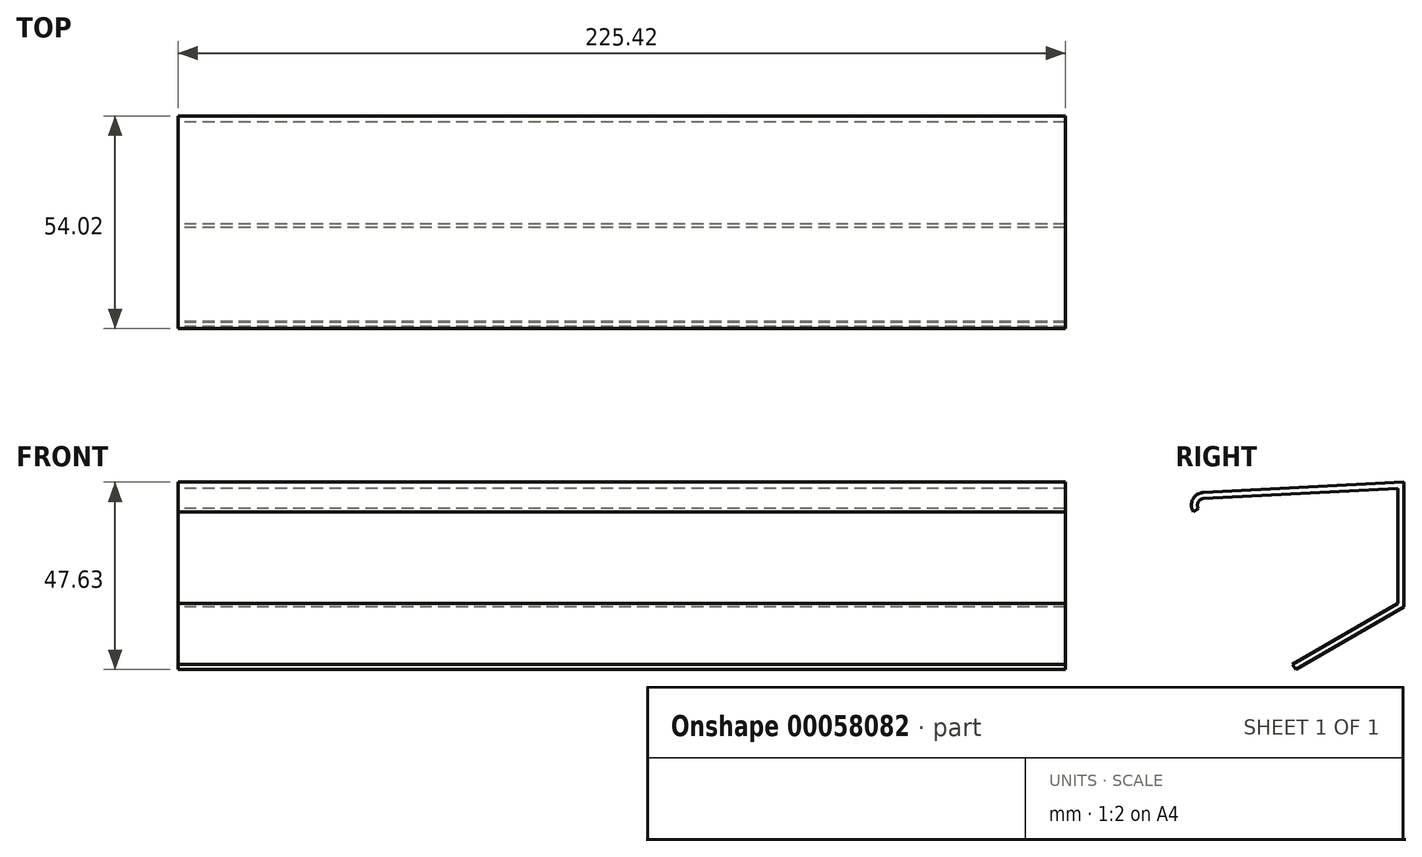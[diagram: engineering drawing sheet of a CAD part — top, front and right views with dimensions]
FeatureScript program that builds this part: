
annotation { "Feature Type Name" : "Feature", "Feature Type Description" : "" }
export const myFeature = defineFeature(function(context is Context, id is Id, definition is map)
    precondition{}
    {
        {
            var Q0;
            Q0=qCreatedBy(makeId("Right.planeOp"),FACE);
            var sketch = newSketch(context, id + "F0", { "sketchPlane" : qUnion([Q0])});
            skLineSegment(sketch, "E0", {"start": v(0, 0) * mm, "end": v(0, 31.75) * mm});
            skLineSegment(sketch, "E1", {"start": v(-56.5, 28.79) * mm, "end": v(-27.5, -15.88) * mm});
            skLineSegment(sketch, "E2", {"start": v(-27.5, -15.87) * mm, "end": v(0, 0) * mm});
            skLineSegment(sketch, "E3", {"start": v(0, 31.75) * mm, "end": v(-56.5, 28.79) * mm});
            skSolve(sketch);
        }
        {
            var Q0;
            Q0=makeQuery(id+"F0.imprint","IMPRINT",FACE,{"disambiguationData":[TD([[makeQuery(id+"F0.imprint","IMPRINT",EDGE,{"derivedFrom":sQuery(id+"F0.wireOp",EDGE,"E0")}),1.0]])]});
            extrude(context, id + "F1", {"entities" : qUnion([Q0]), "endBound" : BoundingType.SYMMETRIC, "depth" : 225.42 * mm});
        }
        {
            var Q0;
            Q0=makeQuery(id+"F1.opExtrude","SWEPT_EDGE",EDGE,{"disambiguationData":[OSD([sQuery(id+"F0.wireOp",EDGE,"E1"),sQuery(id+"F0.wireOp",EDGE,"E3")])]});
            fillet(context, id + "F2", {"entities" : qUnion([Q0]), "radius" : 3.17 * mm, "tangentPropagation" : true, "allowEdgeOverflow" : false});
        }
        {
            var Q0;
            Q0=makeQuery(id+"F1.opExtrude","CAP_FACE",FACE,{"disambiguationData":[OSD([sQuery(id+"F0.wireOp",EDGE,"E0"),sQuery(id+"F0.wireOp",EDGE,"E1"),sQuery(id+"F0.wireOp",EDGE,"E2"),sQuery(id+"F0.wireOp",EDGE,"E3")])],"isStart":false});
            var Q1;
            Q1=makeQuery(id+"F1.opExtrude","SWEPT_FACE",FACE,{"disambiguationData":[OSD([sQuery(id+"F0.wireOp",EDGE,"E1")])]});
            var Q2;
            Q2=makeQuery(id+"F1.opExtrude","CAP_FACE",FACE,{"disambiguationData":[OSD([sQuery(id+"F0.wireOp",EDGE,"E0"),sQuery(id+"F0.wireOp",EDGE,"E1"),sQuery(id+"F0.wireOp",EDGE,"E2"),sQuery(id+"F0.wireOp",EDGE,"E3")])],"isStart":true});
            shell(context, id + "F3", {"entities" : qUnion([Q0, Q1, Q2]), "thickness" : 1.52 * mm});
        }
    });
